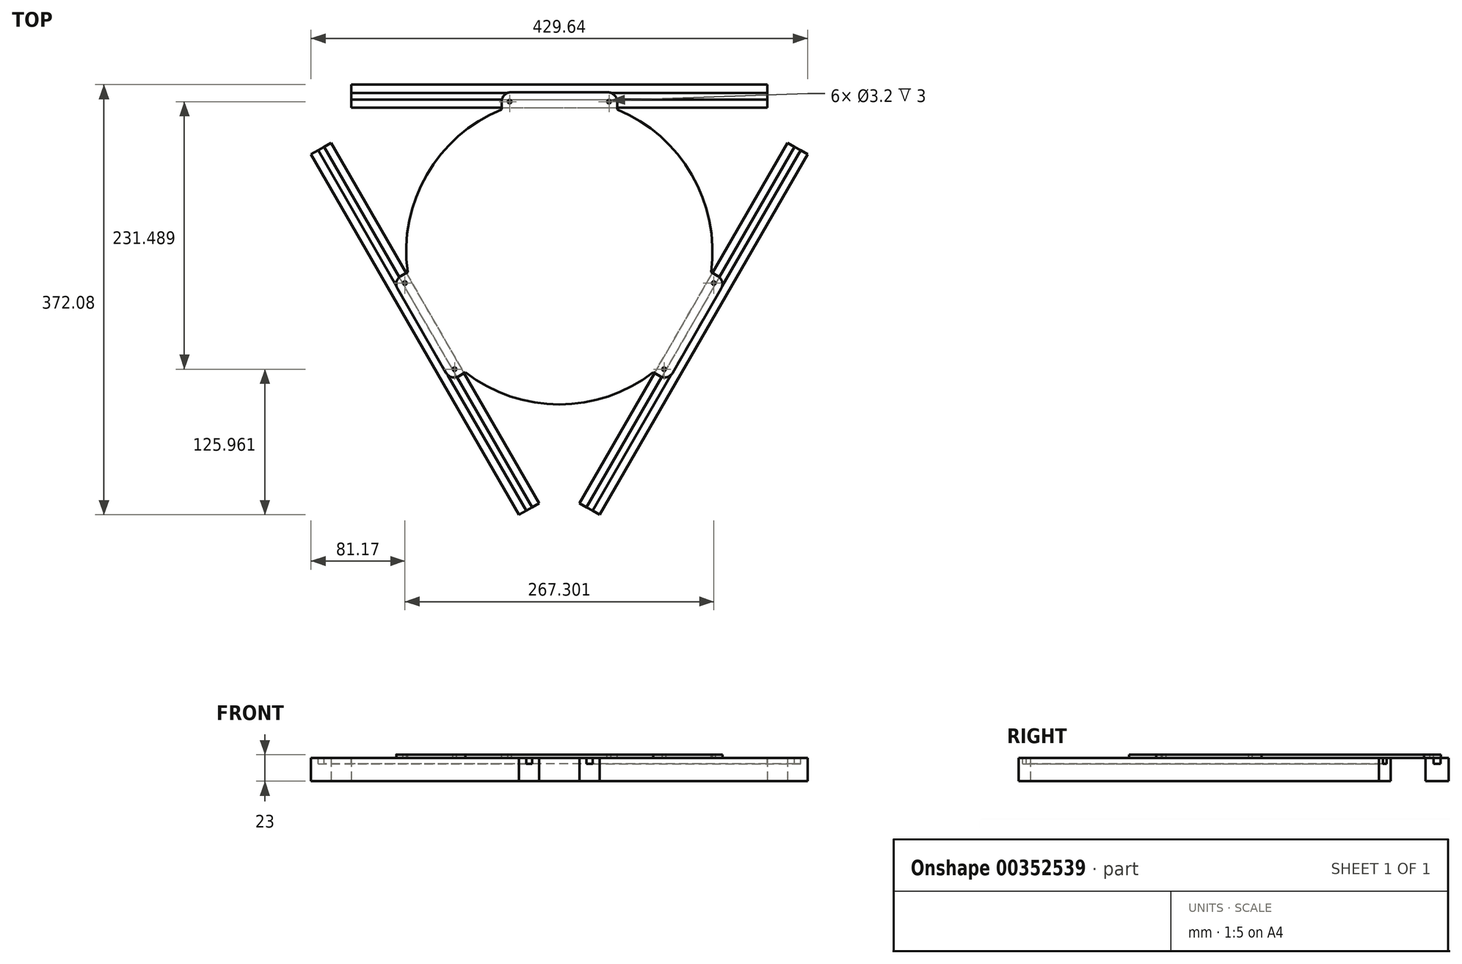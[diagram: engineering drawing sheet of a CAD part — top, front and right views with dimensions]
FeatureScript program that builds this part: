
annotation { "Feature Type Name" : "Feature", "Feature Type Description" : "" }
export const myFeature = defineFeature(function(context is Context, id is Id, definition is map)
    precondition{}
    {
        {
            var Q0;
            Q0=qCreatedBy(makeId("Top.planeOp"),FACE);
            var sketch = newSketch(context, id + "F0", { "sketchPlane" : qUnion([Q0])});
            skLineSegment(sketch, "E0.bottom", {"start": v(0, 0) * mm, "end": v(180, 0) * mm});
            skLineSegment(sketch, "E0.top", {"start": v(0, 20) * mm, "end": v(180, 20) * mm});
            skLineSegment(sketch, "E0.left", {"start": v(0, 0) * mm, "end": v(0, 20) * mm});
            skLineSegment(sketch, "E0.right", {"start": v(180, 0) * mm, "end": v(180, 20) * mm});
            skLineSegment(sketch, "E1.bottom", {"start": v(0, 0) * mm, "end": v(0, 0) * mm});
            skLineSegment(sketch, "E1.top", {"start": v(0, 20) * mm, "end": v(0, 20) * mm});
            skLineSegment(sketch, "E2.bottom", {"start": v(-180, 20) * mm, "end": v(0, 20) * mm});
            skLineSegment(sketch, "E2.top", {"start": v(-180, 0) * mm, "end": v(0, 0) * mm});
            skLineSegment(sketch, "E2.left", {"start": v(-180, 20) * mm, "end": v(-180, 0) * mm});
            skLineSegment(sketch, "E2.right", {"start": v(0, 20) * mm, "end": v(0, 0) * mm});
            skLineSegment(sketch, "E3", {"start": v(-180, 0) * mm, "end": v(-197.5, -30.31) * mm});
            skLineSegment(sketch, "E4.bottom", {"start": v(-197.5, -30.31) * mm, "end": v(-17.5, -342.08) * mm});
            skLineSegment(sketch, "E4.top", {"start": v(-214.82, -40.31) * mm, "end": v(-34.82, -352.08) * mm});
            skLineSegment(sketch, "E4.left", {"start": v(-197.5, -30.31) * mm, "end": v(-214.82, -40.31) * mm});
            skLineSegment(sketch, "E4.right", {"start": v(-17.5, -342.08) * mm, "end": v(-34.82, -352.08) * mm});
            skLineSegment(sketch, "E5", {"start": v(-17.5, -342.08) * mm, "end": v(17.5, -342.08) * mm});
            skLineSegment(sketch, "E6", {"start": v(180, 0) * mm, "end": v(197.5, -30.31) * mm});
            skLineSegment(sketch, "E7", {"start": v(17.5, -342.08) * mm, "end": v(197.5, -30.31) * mm});
            skLineSegment(sketch, "E8", {"start": v(17.5, -342.08) * mm, "end": v(34.82, -352.08) * mm});
            skLineSegment(sketch, "E9", {"start": v(34.82, -352.08) * mm, "end": v(214.82, -40.31) * mm});
            skLineSegment(sketch, "E10", {"start": v(214.82, -40.31) * mm, "end": v(197.5, -30.31) * mm});
            skLineSegment(sketch, "E11", {"start": v(-17.5, -342.08) * mm, "end": v(0, -342.08) * mm});
            skLineSegment(sketch, "E12", {"start": v(0, -342.08) * mm, "end": v(0, 0) * mm});
            skLineSegment(sketch, "E13", {"start": v(197.5, -30.31) * mm, "end": v(188.75, -15.16) * mm});
            skLineSegment(sketch, "E14", {"start": v(-197.5, -30.31) * mm, "end": v(-188.75, -15.16) * mm});
            skLineSegment(sketch, "E15", {"start": v(-197.5, -30.31) * mm, "end": v(-107.5, -186.2) * mm});
            skLineSegment(sketch, "E16", {"start": v(197.5, -30.31) * mm, "end": v(107.5, -186.2) * mm});
            skLineSegment(sketch, "E17", {"start": v(107.5, -186.2) * mm, "end": v(-188.75, -15.16) * mm});
            skLineSegment(sketch, "E18", {"start": v(-107.5, -186.2) * mm, "end": v(188.75, -15.16) * mm});
            skCircle(sketch, "E19", {"center": v(0, -124.13) * mm, "radius": 132.5 * mm});
            skCircle(sketch, "E20", {"center": v(0, -124.13) * mm, "radius": 5 * mm});
            skSolve(sketch);
        }
        {
            var Q0;
            Q0=makeQuery(id+"F0.imprint","IMPRINT",FACE,{"disambiguationData":[TD([[makeQuery(id+"F0.imprint","IMPRINT",EDGE,{"derivedFrom":sQuery(id+"F0.wireOp",EDGE,"E0.bottom")}),1.0]])]});
            var Q1;
            Q1=makeQuery(id+"F0.imprint","IMPRINT",FACE,{"disambiguationData":[TD([[makeQuery(id+"F0.imprint","IMPRINT",EDGE,{"derivedFrom":sQuery(id+"F0.wireOp",EDGE,"E2.bottom")}),-1.0]])]});
            var Q2;
            Q2=makeQuery(id+"F0.imprint","IMPRINT",FACE,{"disambiguationData":[TD([[makeQuery(id+"F0.imprint","IMPRINT",EDGE,{"derivedFrom":sQuery(id+"F0.wireOp",EDGE,"E4.bottom")}),-1.0]])]});
            var Q3;
            Q3=makeQuery(id+"F0.imprint","IMPRINT",FACE,{"disambiguationData":[TD([[makeQuery(id+"F0.imprint","IMPRINT",EDGE,{"derivedFrom":sQuery(id+"F0.wireOp",EDGE,"E7")}),-1.0]])]});
            var Q4;
            {var subQ1=sQuery(id+"F0.wireOp",EDGE,"E0.top");Q4=makeQuery(id+"F0.imprint","IMPRINT",FACE,{"disambiguationData":[TD([[makeQuery(id+"F0.imprint","IMPRINT",EDGE,{"derivedFrom":subQ1}),-1.0]])]});}
            var Q5;
            {var subQ1=sQuery(id+"F0.wireOp",EDGE,"E2.top");var subQ3=sQuery(id+"F0.wireOp",EDGE,"E19");var subQ4=makeQuery(id+"F0.imprint","INTERSECT",VERTEX,{"derivedFrom":[subQ1,subQ3]});Q5=makeQuery(id+"F0.imprint","IMPRINT",FACE,{"disambiguationData":[TD([[makeQuery(id+"F0.imprint","IMPRINT",EDGE,{"disambiguationData":[TD([[subQ4,1.0]])],"derivedFrom":subQ3}),1.0]])]});}
            var Q6;
            {var subQ1=sQuery(id+"F0.wireOp",EDGE,"E8");Q6=makeQuery(id+"F0.imprint","IMPRINT",FACE,{"disambiguationData":[TD([[makeQuery(id+"F0.imprint","IMPRINT",EDGE,{"derivedFrom":subQ1}),1.0]])]});}
            var Q7;
            Q7=makeQuery(id+"F0.imprint","IMPRINT",FACE,{"disambiguationData":[TD([[makeQuery(id+"F0.imprint","IMPRINT",EDGE,{"derivedFrom":sQuery(id+"F0.wireOp",EDGE,"E4.top")}),1.0]])]});
            extrude(context, id + "F1", {"entities" : qUnion([Q0, Q1, Q2, Q3, Q4, Q5, Q6, Q7]), "depth" : 20 * mm});
        }
        {
            var Q0;
            {var subQ1=sQuery(id+"F0.wireOp",EDGE,"E15");var subQ3=sQuery(id+"F0.wireOp",EDGE,"E19");var subQ4=makeQuery(id+"F0.imprint","INTERSECT",VERTEX,{"derivedFrom":[subQ1,subQ3]});Q0=makeQuery(id+"F0.imprint","IMPRINT",FACE,{"disambiguationData":[TD([[makeQuery(id+"F0.imprint","IMPRINT",EDGE,{"disambiguationData":[TD([[subQ4,1.0]])],"derivedFrom":subQ3}),1.0]])]});}
            var Q1;
            {var subQ1=sQuery(id+"F0.wireOp",EDGE,"E2.top");var subQ3=sQuery(id+"F0.wireOp",EDGE,"E19");var subQ4=makeQuery(id+"F0.imprint","INTERSECT",VERTEX,{"derivedFrom":[subQ1,subQ3]});Q1=makeQuery(id+"F0.imprint","IMPRINT",FACE,{"disambiguationData":[TD([[makeQuery(id+"F0.imprint","IMPRINT",EDGE,{"disambiguationData":[TD([[subQ4,-1.0]])],"derivedFrom":subQ3}),1.0]])]});}
            var Q2;
            {var subQ1=sQuery(id+"F0.wireOp",EDGE,"E0.bottom");var subQ3=sQuery(id+"F0.wireOp",EDGE,"E19");var subQ4=makeQuery(id+"F0.imprint","INTERSECT",VERTEX,{"derivedFrom":[subQ1,subQ3]});Q2=makeQuery(id+"F0.imprint","IMPRINT",FACE,{"disambiguationData":[TD([[makeQuery(id+"F0.imprint","IMPRINT",EDGE,{"disambiguationData":[TD([[subQ4,1.0]])],"derivedFrom":subQ3}),1.0]])]});}
            var Q3;
            {var subQ1=sQuery(id+"F0.wireOp",EDGE,"E16");var subQ3=sQuery(id+"F0.wireOp",EDGE,"E19");var subQ4=makeQuery(id+"F0.imprint","INTERSECT",VERTEX,{"derivedFrom":[subQ1,subQ3]});Q3=makeQuery(id+"F0.imprint","IMPRINT",FACE,{"disambiguationData":[TD([[makeQuery(id+"F0.imprint","IMPRINT",EDGE,{"disambiguationData":[TD([[subQ4,-1.0]])],"derivedFrom":subQ3}),1.0]])]});}
            var Q4;
            {var subQ1=sQuery(id+"F0.wireOp",EDGE,"E7");var subQ3=sQuery(id+"F0.wireOp",EDGE,"E19");var subQ4=makeQuery(id+"F0.imprint","INTERSECT",VERTEX,{"derivedFrom":[subQ1,subQ3]});Q4=makeQuery(id+"F0.imprint","IMPRINT",FACE,{"disambiguationData":[TD([[makeQuery(id+"F0.imprint","IMPRINT",EDGE,{"disambiguationData":[TD([[subQ4,1.0]])],"derivedFrom":subQ3}),1.0]])]});}
            var Q5;
            {var subQ1=sQuery(id+"F0.wireOp",EDGE,"E2.top");var subQ3=sQuery(id+"F0.wireOp",EDGE,"E19");var subQ4=makeQuery(id+"F0.imprint","INTERSECT",VERTEX,{"derivedFrom":[subQ1,subQ3]});Q5=makeQuery(id+"F0.imprint","IMPRINT",FACE,{"disambiguationData":[TD([[makeQuery(id+"F0.imprint","IMPRINT",EDGE,{"disambiguationData":[TD([[subQ4,1.0]])],"derivedFrom":subQ3}),1.0]])]});}
            var Q6;
            {var subQ1=sQuery(id+"F0.wireOp",EDGE,"E0.bottom");var subQ3=sQuery(id+"F0.wireOp",EDGE,"E19");var subQ4=makeQuery(id+"F0.imprint","INTERSECT",VERTEX,{"derivedFrom":[subQ1,subQ3]});Q6=makeQuery(id+"F0.imprint","IMPRINT",FACE,{"disambiguationData":[TD([[makeQuery(id+"F0.imprint","IMPRINT",EDGE,{"disambiguationData":[TD([[subQ4,-1.0]])],"derivedFrom":subQ3}),1.0]])]});}
            var Q7;
            {var subQ1=sQuery(id+"F0.wireOp",EDGE,"E7");var subQ3=sQuery(id+"F0.wireOp",EDGE,"E19");var subQ4=makeQuery(id+"F0.imprint","INTERSECT",VERTEX,{"derivedFrom":[subQ1,subQ3]});Q7=makeQuery(id+"F0.imprint","IMPRINT",FACE,{"disambiguationData":[TD([[makeQuery(id+"F0.imprint","IMPRINT",EDGE,{"disambiguationData":[TD([[subQ4,-1.0]])],"derivedFrom":subQ3}),1.0]])]});}
            var Q8;
            {var subQ1=sQuery(id+"F0.wireOp",EDGE,"E4.bottom");var subQ3=sQuery(id+"F0.wireOp",EDGE,"E19");var subQ4=makeQuery(id+"F0.imprint","INTERSECT",VERTEX,{"derivedFrom":[subQ1,subQ3]});Q8=makeQuery(id+"F0.imprint","IMPRINT",FACE,{"disambiguationData":[TD([[makeQuery(id+"F0.imprint","IMPRINT",EDGE,{"disambiguationData":[TD([[subQ4,1.0]])],"derivedFrom":subQ3}),1.0]])]});}
            var Q9;
            {var subQ1=sQuery(id+"F0.wireOp",EDGE,"E4.bottom");var subQ3=sQuery(id+"F0.wireOp",EDGE,"E19");var subQ4=makeQuery(id+"F0.imprint","INTERSECT",VERTEX,{"derivedFrom":[subQ1,subQ3]});Q9=makeQuery(id+"F0.imprint","IMPRINT",FACE,{"disambiguationData":[TD([[makeQuery(id+"F0.imprint","IMPRINT",EDGE,{"disambiguationData":[TD([[subQ4,-1.0]])],"derivedFrom":subQ3}),1.0]])]});}
            var Q10;
            {var subQ0=sQuery(id+"F0.wireOp",EDGE,"E20");var subQ1=sQuery(id+"F0.wireOp",EDGE,"E12");var subQ2=makeQuery(id+"F0.imprint","INTERSECT",VERTEX,{"disambiguationData":[OD(0.0)],"derivedFrom":[subQ1,subQ0]});Q10=makeQuery(id+"F0.imprint","IMPRINT",FACE,{"disambiguationData":[TD([[makeQuery(id+"F0.imprint","IMPRINT",EDGE,{"disambiguationData":[TD([[subQ2,1.0]])],"derivedFrom":subQ0}),1.0]])]});}
            var Q11;
            {var subQ0=sQuery(id+"F0.wireOp",EDGE,"E20");var subQ1=sQuery(id+"F0.wireOp",EDGE,"E17");var subQ2=makeQuery(id+"F0.imprint","INTERSECT",VERTEX,{"disambiguationData":[OD(1.0)],"derivedFrom":[subQ1,subQ0]});Q11=makeQuery(id+"F0.imprint","IMPRINT",FACE,{"disambiguationData":[TD([[makeQuery(id+"F0.imprint","IMPRINT",EDGE,{"disambiguationData":[TD([[subQ2,-1.0]])],"derivedFrom":subQ0}),1.0]])]});}
            var Q12;
            {var subQ0=sQuery(id+"F0.wireOp",EDGE,"E20");var subQ1=sQuery(id+"F0.wireOp",EDGE,"E12");var subQ2=makeQuery(id+"F0.imprint","INTERSECT",VERTEX,{"disambiguationData":[OD(0.0)],"derivedFrom":[subQ1,subQ0]});Q12=makeQuery(id+"F0.imprint","IMPRINT",FACE,{"disambiguationData":[TD([[makeQuery(id+"F0.imprint","IMPRINT",EDGE,{"disambiguationData":[TD([[subQ2,-1.0]])],"derivedFrom":subQ0}),1.0]])]});}
            var Q13;
            {var subQ0=sQuery(id+"F0.wireOp",EDGE,"E20");var subQ1=sQuery(id+"F0.wireOp",EDGE,"E17");var subQ2=makeQuery(id+"F0.imprint","INTERSECT",VERTEX,{"disambiguationData":[OD(0.0)],"derivedFrom":[subQ1,subQ0]});Q13=makeQuery(id+"F0.imprint","IMPRINT",FACE,{"disambiguationData":[TD([[makeQuery(id+"F0.imprint","IMPRINT",EDGE,{"disambiguationData":[TD([[subQ2,-1.0]])],"derivedFrom":subQ0}),1.0]])]});}
            var Q14;
            {var subQ0=sQuery(id+"F0.wireOp",EDGE,"E20");var subQ1=sQuery(id+"F0.wireOp",EDGE,"E12");var subQ2=makeQuery(id+"F0.imprint","INTERSECT",VERTEX,{"disambiguationData":[OD(1.0)],"derivedFrom":[subQ1,subQ0]});Q14=makeQuery(id+"F0.imprint","IMPRINT",FACE,{"disambiguationData":[TD([[makeQuery(id+"F0.imprint","IMPRINT",EDGE,{"disambiguationData":[TD([[subQ2,1.0]])],"derivedFrom":subQ0}),1.0]])]});}
            var Q15;
            {var subQ0=sQuery(id+"F0.wireOp",EDGE,"E20");var subQ1=sQuery(id+"F0.wireOp",EDGE,"E12");var subQ2=makeQuery(id+"F0.imprint","INTERSECT",VERTEX,{"disambiguationData":[OD(1.0)],"derivedFrom":[subQ1,subQ0]});Q15=makeQuery(id+"F0.imprint","IMPRINT",FACE,{"disambiguationData":[TD([[makeQuery(id+"F0.imprint","IMPRINT",EDGE,{"disambiguationData":[TD([[subQ2,-1.0]])],"derivedFrom":subQ0}),1.0]])]});}
            extrude(context, id + "F2", {"entities" : qUnion([Q0, Q1, Q2, Q3, Q4, Q5, Q6, Q7, Q8, Q9, Q10, Q11, Q12, Q13, Q14, Q15]), "depth" : 23 * mm, "hasSecondDirection" : true, "secondDirectionOppositeDirection" : false, "secondDirectionDepth" : 20 * mm});
        }
        {
            var Q0;
            Q0=makeQuery(id+"F2.opExtrude","CAP_FACE",FACE,{"disambiguationData":[OSD([sQuery(id+"F0.wireOp",EDGE,"E19")])],"isStart":false});
            var sketch = newSketch(context, id + "F3", { "sketchPlane" : qUnion([Q0])});
            skCircle(sketch, "E21", {"center": v(0, -124.13) * mm, "radius": 132.5 * mm});
            skLineSegment(sketch, "E22", {"start": v(0, -124.13) * mm, "end": v(0, 8.37) * mm});
            skLineSegment(sketch, "E23", {"start": v(0, 8.37) * mm, "end": v(0, 13.37) * mm});
            skLineSegment(sketch, "E24", {"start": v(0, 13.37) * mm, "end": v(42, 13.37) * mm});
            skLineSegment(sketch, "E25", {"start": v(50, 5.37) * mm, "end": v(50, -1.43) * mm});
            skCircle(sketch, "E26", {"center": v(43, 5.37) * mm, "radius": 1.6 * mm});
            skPoint(sketch, "E27.visualSharp", {"position": v(50, 13.37) * mm});
            skArc(sketch, "E27.filletArc", {"start": v(50, 5.37) * mm, "mid": v(47.66, 11.03) * mm, "end": v(42, 13.37) * mm});
            skLineSegment(sketch, "E28", {"start": v(0, 13.37) * mm, "end": v(-42, 13.37) * mm});
            skLineSegment(sketch, "E29", {"start": v(-50, 5.37) * mm, "end": v(-50, -1.43) * mm});
            skCircle(sketch, "E30", {"center": v(-43, 5.37) * mm, "radius": 1.6 * mm});
            skPoint(sketch, "E31.visualSharp", {"position": v(-50, 13.37) * mm});
            skArc(sketch, "E31.filletArc", {"start": v(-42, 13.37) * mm, "mid": v(-47.66, 11.03) * mm, "end": v(-50, 5.37) * mm});
            skLineSegment(sketch, "E32.1.0", {"start": v(87.15, -232.18) * mm, "end": v(81.26, -228.78) * mm});
            skArc(sketch, "E32.1.1", {"start": v(87.15, -232.18) * mm, "mid": v(93.22, -232.98) * mm, "end": v(98.08, -229.25) * mm});
            skCircle(sketch, "E32.1.2", {"center": v(90.65, -226.12) * mm, "radius": 1.6 * mm});
            skLineSegment(sketch, "E32.1.3", {"start": v(119.08, -192.88) * mm, "end": v(98.08, -229.25) * mm});
            skLineSegment(sketch, "E32.1.4", {"start": v(119.08, -192.88) * mm, "end": v(140.08, -156.5) * mm});
            skArc(sketch, "E32.1.5", {"start": v(140.08, -156.5) * mm, "mid": v(140.88, -150.44) * mm, "end": v(137.15, -145.58) * mm});
            skLineSegment(sketch, "E32.1.6", {"start": v(137.15, -145.58) * mm, "end": v(131.26, -142.18) * mm});
            skCircle(sketch, "E32.1.7", {"center": v(133.65, -151.64) * mm, "radius": 1.6 * mm});
            skLineSegment(sketch, "E32.2.0", {"start": v(-137.15, -145.58) * mm, "end": v(-131.26, -142.18) * mm});
            skArc(sketch, "E32.2.1", {"start": v(-137.15, -145.58) * mm, "mid": v(-140.88, -150.44) * mm, "end": v(-140.08, -156.5) * mm});
            skCircle(sketch, "E32.2.2", {"center": v(-133.65, -151.64) * mm, "radius": 1.6 * mm});
            skLineSegment(sketch, "E32.2.3", {"start": v(-119.08, -192.88) * mm, "end": v(-140.08, -156.5) * mm});
            skLineSegment(sketch, "E32.2.4", {"start": v(-119.08, -192.88) * mm, "end": v(-98.08, -229.25) * mm});
            skArc(sketch, "E32.2.5", {"start": v(-98.08, -229.25) * mm, "mid": v(-93.22, -232.98) * mm, "end": v(-87.15, -232.18) * mm});
            skLineSegment(sketch, "E32.2.6", {"start": v(-87.15, -232.18) * mm, "end": v(-81.26, -228.78) * mm});
            skCircle(sketch, "E32.2.7", {"center": v(-90.65, -226.12) * mm, "radius": 1.6 * mm});
            skLineSegment(sketch, "E32.anchor1", {"start": v(0, -124.13) * mm, "end": v(50, -1.43) * mm, "construction": true});
            skLineSegment(sketch, "E32.anchor2", {"start": v(0, -124.13) * mm, "end": v(-131.26, -142.18) * mm, "construction": true});
            skSolve(sketch);
        }
        {
            var Q0;
            {var subQ1=sQuery(id+"F3.wireOp",EDGE,"E23");Q0=makeQuery(id+"F3.imprint","IMPRINT",FACE,{"disambiguationData":[TD([[makeQuery(id+"F3.imprint","IMPRINT",EDGE,{"derivedFrom":subQ1}),-1.0]])]});}
            var Q1;
            {var subQ1=sQuery(id+"F3.wireOp",EDGE,"E23");Q1=makeQuery(id+"F3.imprint","IMPRINT",FACE,{"disambiguationData":[TD([[makeQuery(id+"F3.imprint","IMPRINT",EDGE,{"derivedFrom":subQ1}),1.0]])]});}
            var Q2;
            {var subQ0=sQuery(id+"F3.wireOp",EDGE,"E21");var subQ1=makeQuery(id+"F3.imprint","INTERSECT",VERTEX,{"derivedFrom":[subQ0,sQuery(id+"F3.wireOp",EDGE,"E23")]});Q2=makeQuery(id+"F3.imprint","IMPRINT",FACE,{"disambiguationData":[TD([[makeQuery(id+"F3.imprint","IMPRINT",EDGE,{"disambiguationData":[TD([[subQ1,1.0]])],"derivedFrom":subQ0}),1.0]])]});}
            var Q3;
            {var subQ0=sQuery(id+"F3.wireOp",EDGE,"E32.1.0");Q3=makeQuery(id+"F3.imprint","IMPRINT",FACE,{"disambiguationData":[TD([[makeQuery(id+"F3.imprint","IMPRINT",EDGE,{"derivedFrom":subQ0}),-1.0]])]});}
            var Q4;
            {var subQ0=sQuery(id+"F3.wireOp",EDGE,"E32.2.0");Q4=makeQuery(id+"F3.imprint","IMPRINT",FACE,{"disambiguationData":[TD([[makeQuery(id+"F3.imprint","IMPRINT",EDGE,{"derivedFrom":subQ0}),-1.0]])]});}
            extrude(context, id + "F4", {"entities" : qUnion([Q0, Q1, Q2, Q3, Q4]), "operationType" : NewBodyOperationType.ADD, "oppositeDirection" : true, "depth" : 3 * mm});
        }
        {
            var Q0;
            Q0=makeQuery(id+"F1.opExtrude","CAP_FACE",FACE,{"disambiguationData":[OSD([sQuery(id+"F0.wireOp",EDGE,"E0.bottom"),sQuery(id+"F0.wireOp",EDGE,"E0.top"),sQuery(id+"F0.wireOp",EDGE,"E0.right"),sQuery(id+"F0.wireOp",EDGE,"E2.bottom"),sQuery(id+"F0.wireOp",EDGE,"E2.top"),sQuery(id+"F0.wireOp",EDGE,"E2.left")])],"isStart":false});
            var sketch = newSketch(context, id + "F5", { "sketchPlane" : qUnion([Q0])});
            skLineSegment(sketch, "E33.bottom", {"start": v(-180, 10) * mm, "end": v(180, 10) * mm});
            skLineSegment(sketch, "E33.top", {"start": v(-180, 7) * mm, "end": v(180, 7) * mm});
            skLineSegment(sketch, "E33.left", {"start": v(-180, 10) * mm, "end": v(-180, 7) * mm});
            skLineSegment(sketch, "E33.right", {"start": v(180, 10) * mm, "end": v(180, 7) * mm});
            skLineSegment(sketch, "E34.bottom", {"start": v(180, 10) * mm, "end": v(-180, 10) * mm});
            skLineSegment(sketch, "E34.top", {"start": v(180, 13) * mm, "end": v(-180, 13) * mm});
            skLineSegment(sketch, "E34.left", {"start": v(180, 10) * mm, "end": v(180, 13) * mm});
            skLineSegment(sketch, "E34.right", {"start": v(-180, 10) * mm, "end": v(-180, 13) * mm});
            skSolve(sketch);
        }
        {
            var Q0;
            Q0=qSketchRegion(id+"F5",true);
            extrude(context, id + "F6", {"entities" : qUnion([Q0]), "oppositeDirection" : true, "depth" : 5 * mm});
        }
        {
            var Q0;
            Q0=makeQuery(id+"F6.opExtrude","SWEPT_BODY",BODY,{"disambiguationData":[OSD([sQuery(id+"F5.wireOp",EDGE,"E33.top"),sQuery(id+"F5.wireOp",EDGE,"E33.left"),sQuery(id+"F5.wireOp",EDGE,"E33.right"),sQuery(id+"F5.wireOp",EDGE,"E34.top"),sQuery(id+"F5.wireOp",EDGE,"E34.left"),sQuery(id+"F5.wireOp",EDGE,"E34.right")])]});
            var Q1;
            Q1=sQuery(id+"F0.wireOp",EDGE,"E20");
            circularPattern(context, id + "F7", {"operationType" : NewBodyOperationType.REMOVE, "entities" : qUnion([Q0]), "axis" : qUnion([Q1]), "angle" : 360 * degree, "instanceCount" : 3, "equalSpace" : true});
        }
    });
